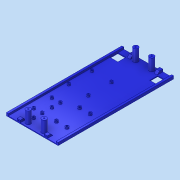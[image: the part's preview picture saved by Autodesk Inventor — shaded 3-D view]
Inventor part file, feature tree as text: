
AUTODESK INVENTOR PART (.ipt)
format: ipt  version: 2022 (Build 260153000, 153)  size: 338,944 bytes
history: native  units: in
note: dims shown in document units (in); Inventor stores cm internally (conversion verified against a paired STEP export)
features: extrude x11, sketch x10, projected_geometry x4, chamfer x1
ambient origin geometry x8: Origin, YZ Plane, XZ Plane, XY Plane, X Axis, Y Axis, Z Axis, Center Point
bodies: Solid1 (feature_tree)
feature tree (26):
  extrude  "Extrusion1"  Depth=11.4173in
  extrude  "Extrusion2"  Depth=0.315in
  chamfer  "Chamfer1"  Distance=0.315in
  extrude  "Extrusion3"  Depth=0.1378in
  extrude  "Extrusion4"  Depth=0.1575in
  extrude  "Extrusion5"  Depth=0.2362in TaperAngle=0.0deg
  extrude  "Extrusion6"  Depth=0.7874in
  extrude  "Extrusion7"  Depth=0.1969in
  extrude  "Extrusion8"  Depth=0.1575in
  extrude  "Extrusion9"  Depth=0.1575in
  extrude  "Extrusion10"  Depth=0.1575in
  extrude  "Extrusion11"  Depth=0.1575in
  sketch  "Sketch1"  dims[d0=5.1181in d1=11.4173in]
  sketch  "Sketch2"  dims[d2=0.0787in d3=0.0in d4=0.315in]
  sketch  "Sketch3"  dims[d5=0.5512in]
  sketch  "Sketch4"  dims[d6=1.1811in d7=0.315in d8=0.0in]
  sketch  "Sketch5"  dims[d9=0.2362in d10=0.0787in d11=45.0deg d12=0.1378in]
  sketch  "Sketch6"  dims[d13=0.1575in d14=0.1575in]
  sketch  "Sketch8"  dims[d15=0.2362in d16=0.0in d17=0.2362in d18=0.0in]
  sketch  "Sketch9"  dims[d19=0.7874in d20=0.7874in]
  projected_geometry  "Projected Loop1"
  projected_geometry  "Projected Loop2"
  projected_geometry  "Projected Loop3"
  projected_geometry  "Projected Loop4"
  sketch  "Sketch10"  dims[d21=0.5906in d22=0.1969in]
  sketch  "Sketch11"  dims[d23=0.2362in d24=0.0in d25=1.9291in d26=2.2835in d28=2.2047in d29=3.3465in d30=0.1378in d31=0.1378in d32=1.1811in d33=0.1378in d34=0.1378in d35=0.1378in d36=0.1378in d37=0.1575in d38=0.0in d39=1.0in d40=0.3937in d41=1.0in d42=1.0in d57=0.83in d58=0.83in d61=0.1378in d62=0.2756in d63=0.1378in d64=0.2756in d65=0.1378in d66=0.2756in d67=0.83in d68=0.83in d71=0.1378in d72=0.2756in d73=0.1378in d74=0.2756in d76=0.2756in d77=0.1575in d78=0.0in d79=0.3937in d80=0.4724in d81=0.3937in d82=1.5748in d83=1.1811in d84=0.0in d85=0.128in d86=0.3937in d87=0.0in d88=0.1969in d89=0.0in d91=0.7874in d92=0.7874in d93=1.0433in d94=2.3031in d95=0.7874in d96=1.811in d97=2.5591in d98=1.1811in d99=0.1772in d100=0.315in d101=0.1772in d102=0.315in d103=0.1772in d104=0.315in d105=0.1772in d106=0.315in d107=0.1575in d108=0.0in]
